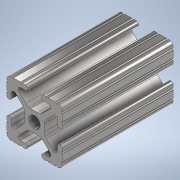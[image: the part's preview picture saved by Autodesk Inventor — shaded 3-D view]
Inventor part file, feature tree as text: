
AUTODESK INVENTOR PART (.ipt)
format: ipt  version: 2020 (Build 240168000, 168)  size: 246,272 bytes
history: native  units: in
note: dims shown in document units (in); Inventor stores cm internally (conversion verified against a paired STEP export)
features: extrude x1, sketch x1
ambient origin geometry x8: Origin, YZ Plane, XZ Plane, XY Plane, X Axis, Y Axis, Z Axis, Center Point
bodies: Solid1 (feature_tree)
feature tree (2):
  extrude  "Extrusion1"  [1 undecoded]
  sketch  "Sketch1"  dims[d0=2.0in d1=0.0in]
note: 1 required parameter value undecoded (feature->parameter linkage not recoverable at this tier; creation-order binding heuristic only, values carry confidence <= 0.55)
